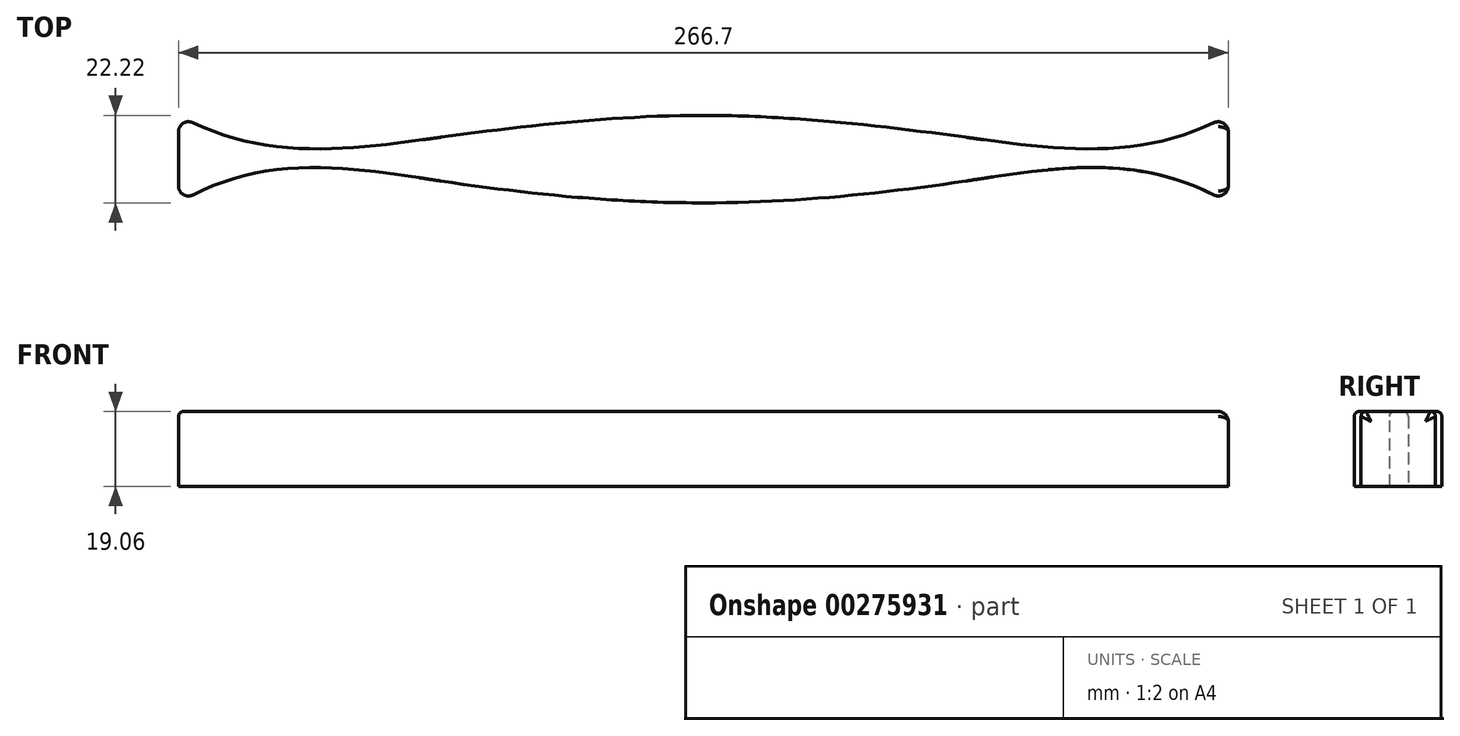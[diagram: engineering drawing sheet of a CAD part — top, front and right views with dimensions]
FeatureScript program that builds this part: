
annotation { "Feature Type Name" : "Feature", "Feature Type Description" : "" }
export const myFeature = defineFeature(function(context is Context, id is Id, definition is map)
    precondition{}
    {
        {
            var Q0;
            Q0=qCreatedBy(makeId("Top.planeOp"),FACE);
            var sketch = newSketch(context, id + "F0", { "sketchPlane" : qUnion([Q0])});
            skLineSegment(sketch, "E0", {"start": v(0, 0) * mm, "end": v(0, 11.11) * mm});
            skLineSegment(sketch, "E1", {"start": v(0, 0) * mm, "end": v(-133.35, 0) * mm});
            skLineSegment(sketch, "E2", {"start": v(0, 0) * mm, "end": v(133.35, 0) * mm});
            skLineSegment(sketch, "E3", {"start": v(-133.35, 0) * mm, "end": v(-133.35, 11.11) * mm});
            skLineSegment(sketch, "E4", {"start": v(-133.35, 0) * mm, "end": v(-133.35, -11.11) * mm});
            skLineSegment(sketch, "E5", {"start": v(133.35, 0) * mm, "end": v(133.35, 11.11) * mm});
            skLineSegment(sketch, "E6", {"start": v(133.35, 0) * mm, "end": v(133.35, -11.11) * mm});
            skLineSegment(sketch, "E7", {"start": v(0, 0) * mm, "end": v(-66.68, 0) * mm});
            skLineSegment(sketch, "E8", {"start": v(0, 0) * mm, "end": v(66.68, 0) * mm});
            skLineSegment(sketch, "E9", {"start": v(-66.68, 0) * mm, "end": v(-66.68, 5.56) * mm});
            skLineSegment(sketch, "E10", {"start": v(-66.68, 0) * mm, "end": v(-66.68, -5.56) * mm});
            skLineSegment(sketch, "E11", {"start": v(66.68, 0) * mm, "end": v(66.68, 5.56) * mm});
            skLineSegment(sketch, "E12", {"start": v(66.68, 0) * mm, "end": v(66.68, -5.56) * mm});
            skFitSpline(sketch, "E13", {"points": [v(-133.35, 11.11) * mm, v(-66.68, 5.56) * mm, v(0, 11.11) * mm, v(66.68, 5.56) * mm, v(133.35, 11.11) * mm], "startDerivative": vector(265.11, -145.76) * mm, "endDerivative": vector(265.11, 145.76) * mm});
            skFitSpline(sketch, "E14", {"points": [v(-133.35, -11.11) * mm, v(-66.68, -5.56) * mm, v(0, -11.11) * mm, v(66.68, -5.56) * mm, v(133.35, -11.11) * mm], "startDerivative": vector(268.52, 158.96) * mm, "endDerivative": vector(268.52, -158.96) * mm});
            skLineSegment(sketch, "E15", {"start": v(0, 0) * mm, "end": v(0, -11.11) * mm});
            skSolve(sketch);
        }
        {
            var Q0;
            Q0=makeQuery(id+"F0.imprint","IMPRINT",FACE,{"disambiguationData":[TD([[makeQuery(id+"F0.imprint","IMPRINT",EDGE,{"derivedFrom":sQuery(id+"F0.wireOp",EDGE,"E1")}),-1.0]])]});
            var Q1;
            Q1=makeQuery(id+"F0.imprint","IMPRINT",FACE,{"disambiguationData":[TD([[makeQuery(id+"F0.imprint","IMPRINT",EDGE,{"derivedFrom":sQuery(id+"F0.wireOp",EDGE,"E1")}),1.0]])]});
            var Q2;
            {var subQ0=sQuery(id+"F0.wireOp",EDGE,"E0");Q2=makeQuery(id+"F0.imprint","IMPRINT",FACE,{"disambiguationData":[TD([[makeQuery(id+"F0.imprint","IMPRINT",EDGE,{"derivedFrom":subQ0}),1.0]])]});}
            var Q3;
            Q3=makeQuery(id+"F0.imprint","IMPRINT",FACE,{"disambiguationData":[TD([[makeQuery(id+"F0.imprint","IMPRINT",EDGE,{"derivedFrom":sQuery(id+"F0.wireOp",EDGE,"E7")}),1.0]])]});
            var Q4;
            {var subQ0=sQuery(id+"F0.wireOp",EDGE,"E0");Q4=makeQuery(id+"F0.imprint","IMPRINT",FACE,{"disambiguationData":[TD([[makeQuery(id+"F0.imprint","IMPRINT",EDGE,{"derivedFrom":subQ0}),-1.0]])]});}
            var Q5;
            Q5=makeQuery(id+"F0.imprint","IMPRINT",FACE,{"disambiguationData":[TD([[makeQuery(id+"F0.imprint","IMPRINT",EDGE,{"derivedFrom":sQuery(id+"F0.wireOp",EDGE,"E8")}),-1.0]])]});
            var Q6;
            Q6=makeQuery(id+"F0.imprint","IMPRINT",FACE,{"disambiguationData":[TD([[makeQuery(id+"F0.imprint","IMPRINT",EDGE,{"derivedFrom":sQuery(id+"F0.wireOp",EDGE,"E2")}),-1.0]])]});
            var Q7;
            Q7=makeQuery(id+"F0.imprint","IMPRINT",FACE,{"disambiguationData":[TD([[makeQuery(id+"F0.imprint","IMPRINT",EDGE,{"derivedFrom":sQuery(id+"F0.wireOp",EDGE,"E2")}),1.0]])]});
            extrude(context, id + "F1", {"entities" : qUnion([Q0, Q1, Q2, Q3, Q4, Q5, Q6, Q7]), "endBound" : BoundingType.SYMMETRIC, "depth" : 19.05 * mm});
        }
        {
            var Q0;
            Q0=makeQuery(id+"F1.opExtrude","CAP_EDGE",EDGE,{"disambiguationData":[OSD([sQuery(id+"F0.wireOp",EDGE,"E14")])],"isStart":false});
            var Q1;
            Q1=makeQuery(id+"F1.opExtrude","CAP_EDGE",EDGE,{"disambiguationData":[OSD([sQuery(id+"F0.wireOp",EDGE,"E3"),sQuery(id+"F0.wireOp",EDGE,"E4")])],"isStart":false});
            var Q2;
            Q2=makeQuery(id+"F1.opExtrude","CAP_EDGE",EDGE,{"disambiguationData":[OSD([sQuery(id+"F0.wireOp",EDGE,"E13")])],"isStart":false});
            fillet(context, id + "F2", {"entities" : qUnion([Q0, Q1, Q2]), "radius" : 1.27 * mm, "tangentPropagation" : true, "allowEdgeOverflow" : false});
        }
        {
            var Q0;
            Q0=makeQuery(id+"F1.opExtrude","SWEPT_EDGE",EDGE,{"disambiguationData":[OSD([sQuery(id+"F0.wireOp",EDGE,"E4"),sQuery(id+"F0.wireOp",EDGE,"E14")])]});
            var Q1;
            Q1=makeQuery(id+"F1.opExtrude","SWEPT_EDGE",EDGE,{"disambiguationData":[OSD([sQuery(id+"F0.wireOp",EDGE,"E3"),sQuery(id+"F0.wireOp",EDGE,"E13")])]});
            var Q2;
            Q2=makeQuery(id+"F1.opExtrude","SWEPT_EDGE",EDGE,{"disambiguationData":[OSD([sQuery(id+"F0.wireOp",EDGE,"E6"),sQuery(id+"F0.wireOp",EDGE,"E14")])]});
            fillet(context, id + "F3", {"entities" : qUnion([Q0, Q1, Q2]), "radius" : 2.54 * mm, "tangentPropagation" : true, "allowEdgeOverflow" : false});
        }
    });
